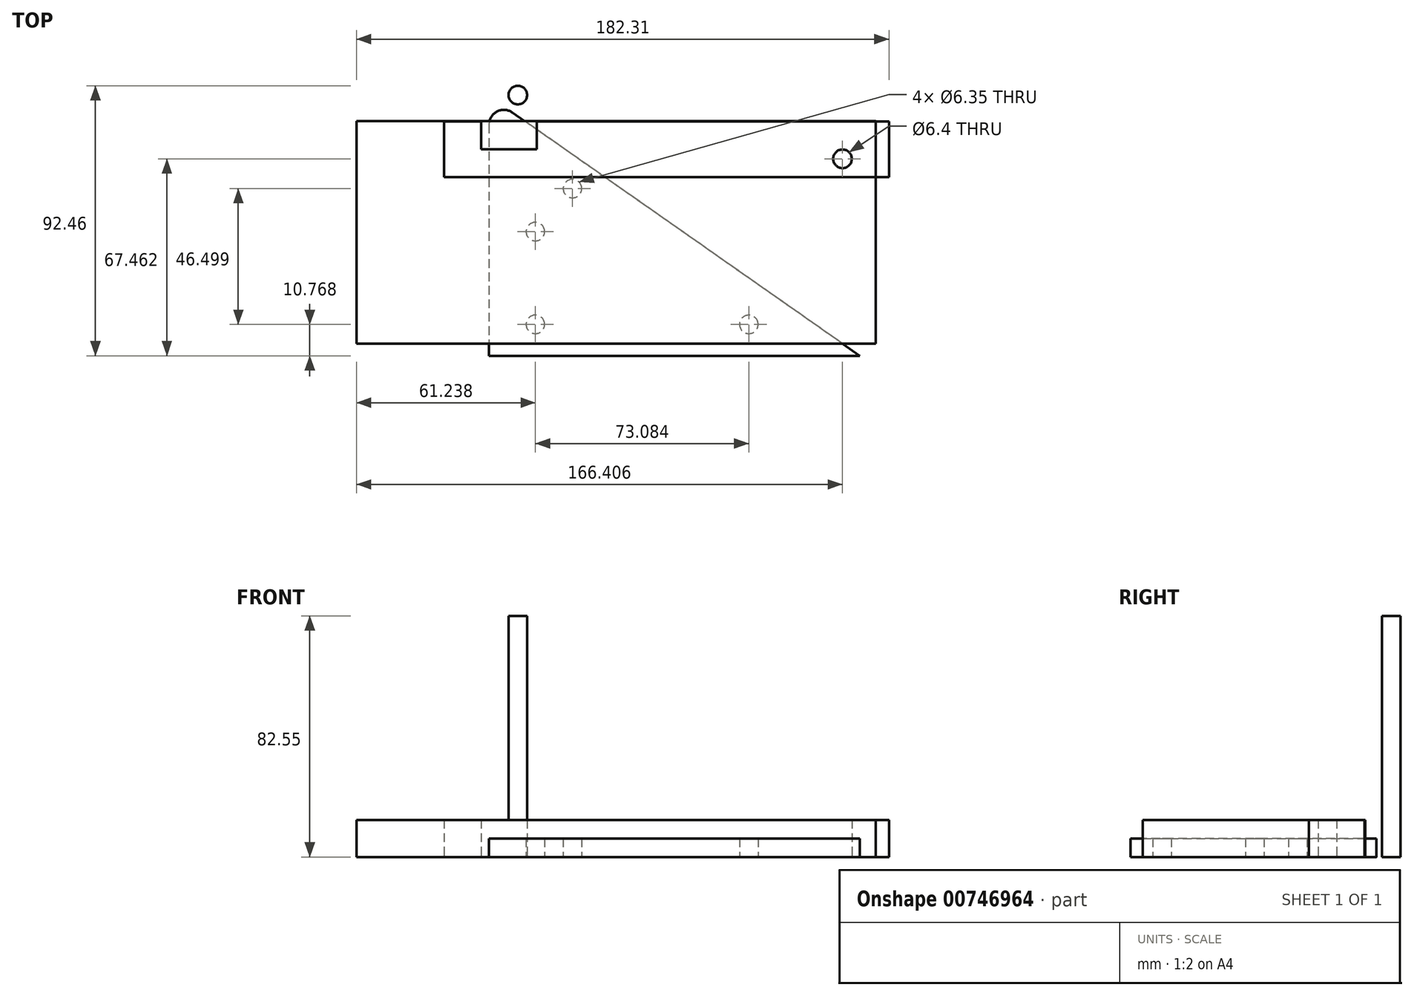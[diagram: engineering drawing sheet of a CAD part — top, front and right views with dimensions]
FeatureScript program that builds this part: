
annotation { "Feature Type Name" : "Feature", "Feature Type Description" : "" }
export const myFeature = defineFeature(function(context is Context, id is Id, definition is map)
    precondition{}
    {
        {
            var Q0;
            Q0=qCreatedBy(makeId("Top.planeOp"),FACE);
            var sketch = newSketch(context, id + "F0", { "sketchPlane" : qUnion([Q0])});
            skCircle(sketch, "E0", {"center": v(-37.94, 46.75) * mm, "radius": 3.18 * mm});
            skSolve(sketch);
        }
        {
            var Q0;
            Q0 = qSketchRegion(id + "F0", true);
            extrude(context, id + "F1", {"entities" : qUnion([Q0]), "depth" : 82.55 * mm, "offsetDistance" : 25.4 * mm});
        }
        {
            var Q0;
            Q0=qCreatedBy(makeId("Top.planeOp"),FACE);
            var sketch = newSketch(context, id + "F2", { "sketchPlane" : qUnion([Q0])});
            skLineSegment(sketch, "E1.bottom", {"start": v(-93.16, 37.84) * mm, "end": v(84.64, 37.84) * mm});
            skLineSegment(sketch, "E1.top", {"start": v(-93.16, -38.36) * mm, "end": v(84.64, -38.36) * mm});
            skLineSegment(sketch, "E1.left", {"start": v(-93.16, 37.84) * mm, "end": v(-93.16, -38.36) * mm});
            skLineSegment(sketch, "E1.right", {"start": v(84.64, 37.84) * mm, "end": v(84.64, -38.36) * mm});
            skSolve(sketch);
        }
        {
            var Q0;
            Q0=makeQuery(id+"F2.imprint","IMPRINT",FACE,{"disambiguationData":[TD([[makeQuery(id+"F2.imprint","IMPRINT",EDGE,{"derivedFrom":sQuery(id+"F2.wireOp",EDGE,"E1.bottom")}),-1.0]])]});
            extrude(context, id + "F3", {"entities" : qUnion([Q0]), "depth" : 12.7 * mm, "offsetDistance" : 25.4 * mm});
        }
        {
            var Q0;
            Q0=qCreatedBy(makeId("Top.planeOp"),FACE);
            var sketch = newSketch(context, id + "F4", { "sketchPlane" : qUnion([Q0])});
            skLineSegment(sketch, "E2", {"start": v(-47.8, 46.37) * mm, "end": v(-47.8, -42.53) * mm});
            skLineSegment(sketch, "E3", {"start": v(-47.8, -42.53) * mm, "end": v(79.2, -42.53) * mm});
            skLineSegment(sketch, "E4", {"start": v(79.2, -42.53) * mm, "end": v(-47.8, 46.37) * mm});
            skCircle(sketch, "E5", {"center": v(41.16, -31.76) * mm, "radius": 3.18 * mm});
            skCircle(sketch, "E6", {"center": v(-31.92, -31.75) * mm, "radius": 3.18 * mm});
            skCircle(sketch, "E7", {"center": v(-31.92, 0) * mm, "radius": 3.18 * mm});
            skCircle(sketch, "E8", {"center": v(-19.22, 14.74) * mm, "radius": 3.18 * mm});
            skSolve(sketch);
        }
        {
            var Q0;
            Q0=makeQuery(id+"F4.imprint","IMPRINT",FACE,{"disambiguationData":[TD([[makeQuery(id+"F4.imprint","IMPRINT",EDGE,{"derivedFrom":sQuery(id+"F4.wireOp",EDGE,"E2")}),1.0]])]});
            extrude(context, id + "F5", {"entities" : qUnion([Q0]), "depth" : 6.35 * mm, "offsetDistance" : 25.4 * mm});
        }
        {
            var Q0;
            Q0=makeQuery(id+"F5.opExtrude","SWEPT_EDGE",EDGE,{"disambiguationData":[OSD([sQuery(id+"F4.wireOp",EDGE,"E2"),sQuery(id+"F4.wireOp",EDGE,"E4")])]});
            fillet(context, id + "F6", {"entities" : qUnion([Q0]), "radius" : 5.08 * mm, "tangentPropagation" : true, "allowEdgeOverflow" : false});
        }
        {
            var Q0;
            Q0=qCreatedBy(makeId("Top.planeOp"),FACE);
            var sketch = newSketch(context, id + "F7", { "sketchPlane" : qUnion([Q0])});
            skLineSegment(sketch, "E9.bottom", {"start": v(-63.25, 37.66) * mm, "end": v(89.15, 37.66) * mm});
            skLineSegment(sketch, "E9.top", {"start": v(-63.25, 18.6) * mm, "end": v(89.15, 18.6) * mm});
            skLineSegment(sketch, "E9.left", {"start": v(-63.25, 37.66) * mm, "end": v(-63.25, 18.6) * mm});
            skLineSegment(sketch, "E9.right", {"start": v(89.15, 37.66) * mm, "end": v(89.15, 18.6) * mm});
            skLineSegment(sketch, "E10.bottom", {"start": v(-50.55, 37.66) * mm, "end": v(-31.5, 37.66) * mm});
            skLineSegment(sketch, "E10.top", {"start": v(-50.55, 28.13) * mm, "end": v(-31.5, 28.13) * mm});
            skLineSegment(sketch, "E10.left", {"start": v(-50.55, 37.66) * mm, "end": v(-50.55, 28.13) * mm});
            skLineSegment(sketch, "E10.right", {"start": v(-31.5, 37.66) * mm, "end": v(-31.5, 28.13) * mm});
            skCircle(sketch, "E11", {"center": v(73.25, 24.93) * mm, "radius": 3.2 * mm});
            skSolve(sketch);
        }
        {
            var Q0;
            Q0=makeQuery(id+"F7.imprint","IMPRINT",FACE,{"disambiguationData":[TD([[makeQuery(id+"F7.imprint","IMPRINT",EDGE,{"derivedFrom":sQuery(id+"F7.wireOp",EDGE,"E9.top")}),1.0]])]});
            extrude(context, id + "F8", {"entities" : qUnion([Q0]), "depth" : 12.7 * mm, "offsetDistance" : 25.4 * mm});
        }
    });
